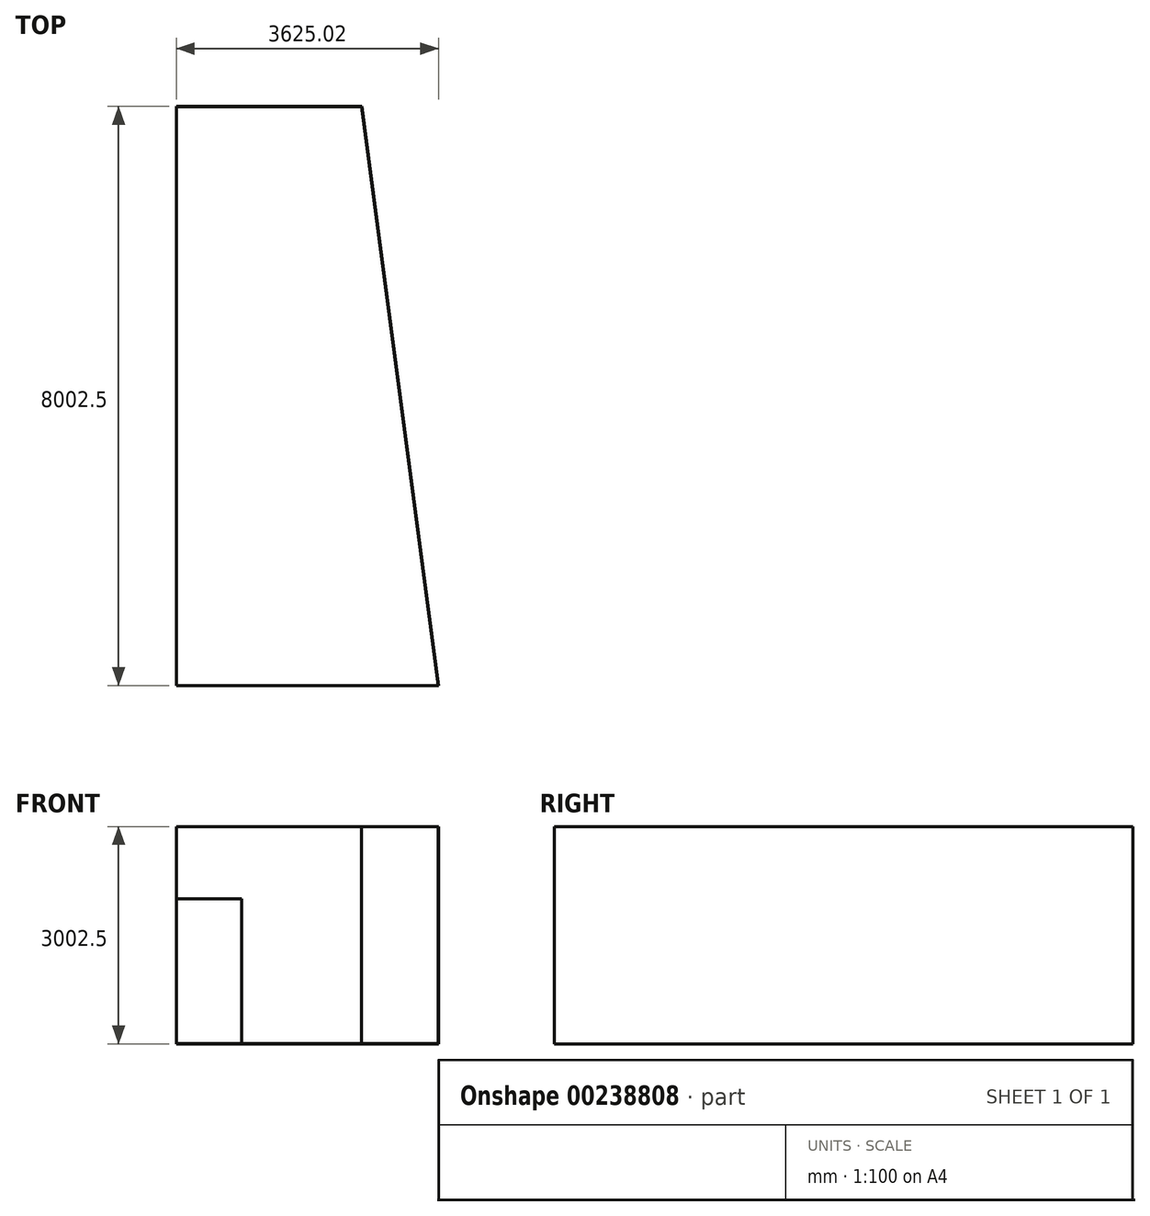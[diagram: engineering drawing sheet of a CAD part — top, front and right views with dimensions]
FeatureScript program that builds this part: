
annotation { "Feature Type Name" : "Feature", "Feature Type Description" : "" }
export const myFeature = defineFeature(function(context is Context, id is Id, definition is map)
    precondition{}
    {
        {
            var Q0;
            Q0=qCreatedBy(makeId("Top.planeOp"),FACE);
            var sketch = newSketch(context, id + "F0", { "sketchPlane" : qUnion([Q0])});
            skLineSegment(sketch, "E0", {"start": v(0, 0) * mm, "end": v(0, 8000) * mm});
            skLineSegment(sketch, "E1", {"start": v(0, 8000) * mm, "end": v(2560, 8000) * mm});
            skLineSegment(sketch, "E2", {"start": v(2560, 8000) * mm, "end": v(3620, 0) * mm});
            skLineSegment(sketch, "E3", {"start": v(3620, 0) * mm, "end": v(0, 0) * mm});
            skSolve(sketch);
        }
        {
            var Q0;
            Q0 = qSketchRegion(id + "F0", true);
            extrude(context, id + "F1", {"entities" : qUnion([Q0]), "depth" : 3000 * mm});
        }
        {
            var Q0;
            Q0=makeQuery(id+"F1.opExtrude","CAP_FACE",FACE,{"disambiguationData":[OSD([sQuery(id+"F0.wireOp",EDGE,"E0"),sQuery(id+"F0.wireOp",EDGE,"E1"),sQuery(id+"F0.wireOp",EDGE,"E2"),sQuery(id+"F0.wireOp",EDGE,"E3")])],"isStart":false});
            var Q1;
            Q1=makeQuery(id+"F1.opExtrude","SWEPT_FACE",FACE,{"disambiguationData":[OSD([sQuery(id+"F0.wireOp",EDGE,"E3")])]});
            shell(context, id + "F2", {"entities" : qUnion([Q0, Q1]), "thickness" : 2.5 * mm, "oppositeDirection" : true});
        }
        {
            var Q0;
            Q0=makeQuery(id+"F2.opShell","OFFSET_FACE",FACE,{"disambiguationData":[OSD([sQuery(id+"F0.wireOp",EDGE,"E1")])]});
            var sketch = newSketch(context, id + "F3", { "sketchPlane" : qUnion([Q0])});
            skLineSegment(sketch, "E4.bottom", {"start": v(0, 0) * mm, "end": v(900, 0) * mm});
            skLineSegment(sketch, "E4.top", {"start": v(0, 2000) * mm, "end": v(900, 2000) * mm});
            skLineSegment(sketch, "E4.left", {"start": v(0, 0) * mm, "end": v(0, 2000) * mm});
            skLineSegment(sketch, "E4.right", {"start": v(900, 0) * mm, "end": v(900, 2000) * mm});
            skSolve(sketch);
        }
        {
            var Q0;
            Q0 = qSketchRegion(id + "F3", true);
            extrude(context, id + "F4", {"entities" : qUnion([Q0]), "operationType" : NewBodyOperationType.REMOVE, "oppositeDirection" : true, "depth" : 25 * mm});
        }
    });
